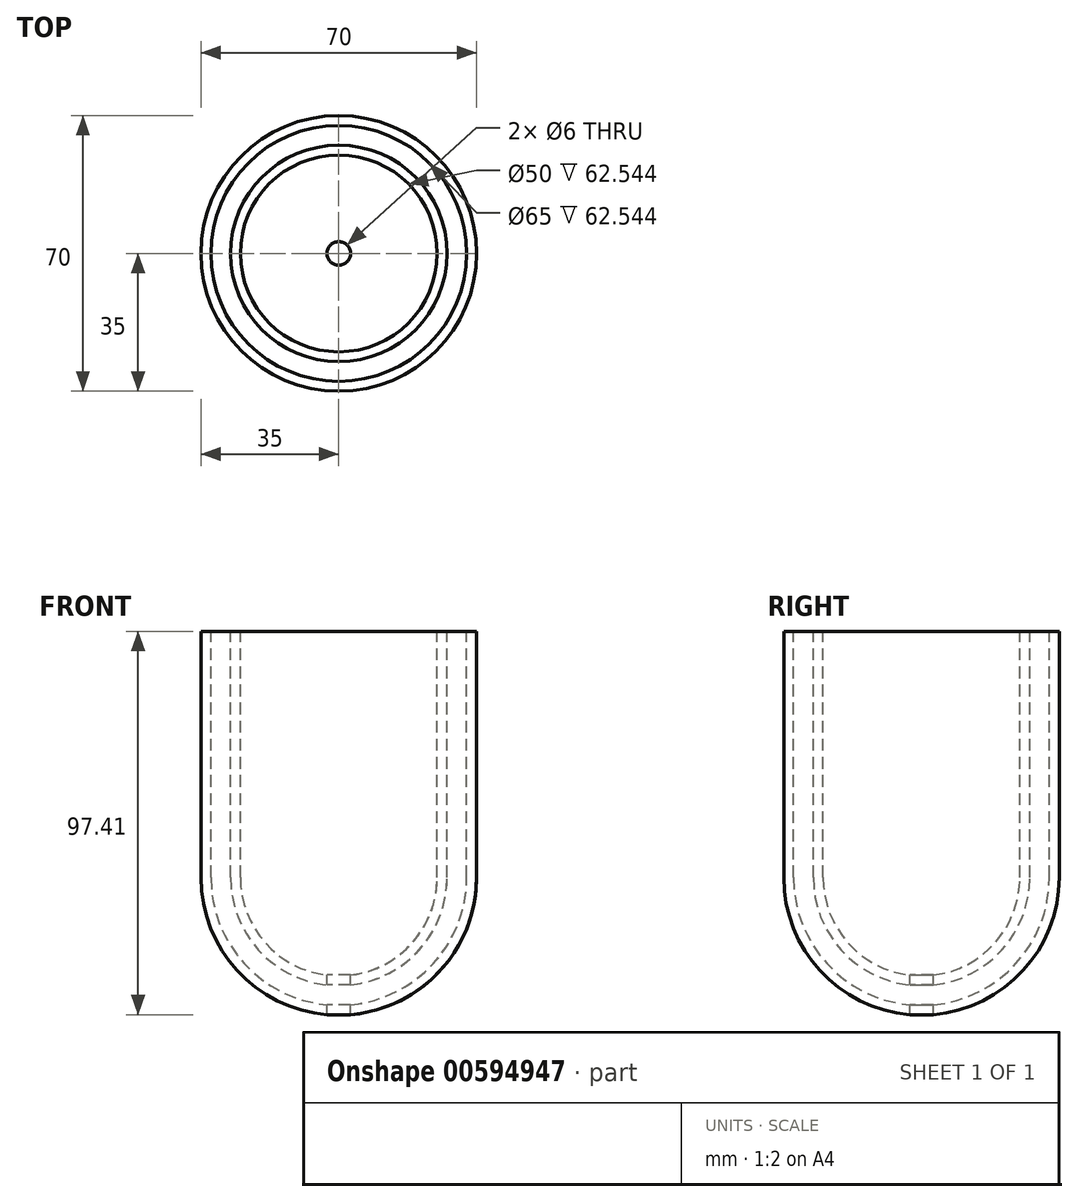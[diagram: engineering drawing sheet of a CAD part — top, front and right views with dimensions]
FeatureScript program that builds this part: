
annotation { "Feature Type Name" : "Feature", "Feature Type Description" : "" }
export const myFeature = defineFeature(function(context is Context, id is Id, definition is map)
    precondition{}
    {
        {
            var Q0;
            Q0=qCreatedBy(makeId("Front.planeOp"),FACE);
            var sketch = newSketch(context, id + "F0", { "sketchPlane" : qUnion([Q0])});
            skCircle(sketch, "E0", {"center": v(0, 0) * mm, "radius": 32.5 * mm, "construction": true});
            skCircle(sketch, "E1", {"center": v(0, 0) * mm, "radius": 35 * mm, "construction": true});
            skCircle(sketch, "E2", {"center": v(0, 0) * mm, "radius": 25 * mm, "construction": true});
            skCircle(sketch, "E3", {"center": v(0, 0) * mm, "radius": 27.5 * mm, "construction": true});
            skArc(sketch, "E4", {"start": v(-25, 0) * mm, "mid": v(0, -25) * mm, "end": v(25, 0) * mm});
            skArc(sketch, "E5", {"start": v(-27.5, 0) * mm, "mid": v(0, -27.5) * mm, "end": v(27.5, 0) * mm});
            skArc(sketch, "E6", {"start": v(-32.5, 0) * mm, "mid": v(0, -32.5) * mm, "end": v(32.5, 0) * mm});
            skArc(sketch, "E7", {"start": v(-35, 0) * mm, "mid": v(0, -35) * mm, "end": v(35, 0) * mm});
            skLineSegment(sketch, "E8", {"start": v(-35, 0) * mm, "end": v(-35, 62.54) * mm});
            skLineSegment(sketch, "E9", {"start": v(-32.5, 0) * mm, "end": v(-32.5, 62.54) * mm});
            skLineSegment(sketch, "E10", {"start": v(-27.5, 0) * mm, "end": v(-27.5, 62.54) * mm});
            skLineSegment(sketch, "E11", {"start": v(-25, 0) * mm, "end": v(-25, 62.54) * mm});
            skLineSegment(sketch, "E12", {"start": v(25, 0) * mm, "end": v(25, 62.54) * mm});
            skLineSegment(sketch, "E13", {"start": v(27.5, 0) * mm, "end": v(27.5, 62.54) * mm});
            skLineSegment(sketch, "E14", {"start": v(32.5, 0) * mm, "end": v(32.5, 62.54) * mm});
            skLineSegment(sketch, "E15", {"start": v(35, 0) * mm, "end": v(35, 62.63) * mm});
            skPoint(sketch, "E16", {"position": v(0, -25) * mm});
            skPoint(sketch, "E17", {"position": v(0, -27.5) * mm});
            skPoint(sketch, "E18", {"position": v(0, -32.5) * mm});
            skPoint(sketch, "E19", {"position": v(0, -35) * mm});
            skLineSegment(sketch, "E20.bottom", {"start": v(-3, -16) * mm, "end": v(3, -16) * mm});
            skLineSegment(sketch, "E20.top", {"start": v(-3, -42) * mm, "end": v(3, -42) * mm});
            skLineSegment(sketch, "E20.left", {"start": v(-3, -16) * mm, "end": v(-3, -42) * mm});
            skLineSegment(sketch, "E20.right", {"start": v(3, -16) * mm, "end": v(3, -42) * mm});
            skLineSegment(sketch, "E21", {"start": v(-35, 62.54) * mm, "end": v(35, 62.54) * mm});
            skLineSegment(sketch, "E22", {"start": v(-35, 57.54) * mm, "end": v(35, 57.54) * mm});
            skLineSegment(sketch, "E23", {"start": v(0, 100.78) * mm, "end": v(0, -81.22) * mm, "construction": true});
            skPoint(sketch, "E23.startSnap0", {"position": v(0, 62.54) * mm});
            skArc(sketch, "E24", {"start": v(-35, 62.54) * mm, "mid": v(0, 97.54) * mm, "end": v(35, 62.54) * mm});
            skArc(sketch, "E25", {"start": v(-25, 62.54) * mm, "mid": v(0, 87.54) * mm, "end": v(25, 62.54) * mm});
            skArc(sketch, "E26", {"start": v(-27.5, 62.54) * mm, "mid": v(0, 90.04) * mm, "end": v(27.5, 62.54) * mm});
            skArc(sketch, "E27", {"start": v(32.5, 62.54) * mm, "mid": v(0, 95.04) * mm, "end": v(-32.5, 62.54) * mm});
            skPoint(sketch, "E28", {"position": v(0, 97.54) * mm});
            skPoint(sketch, "E29", {"position": v(0, 95.04) * mm});
            skPoint(sketch, "E30", {"position": v(0, 90.04) * mm});
            skPoint(sketch, "E31", {"position": v(0, 87.54) * mm});
            skSolve(sketch);
        }
        {
            var Q0;
            {var subQ1=sQuery(id+"F0.wireOp",EDGE,"E10");var subQ3=sQuery(id+"F0.wireOp",EDGE,"E22");var subQ4=makeQuery(id+"F0.imprint","INTERSECT",VERTEX,{"derivedFrom":[subQ1,subQ3]});Q0=makeQuery(id+"F0.imprint","IMPRINT",FACE,{"disambiguationData":[TD([[makeQuery(id+"F0.imprint","IMPRINT",EDGE,{"disambiguationData":[TD([[subQ4,-1.0]])],"derivedFrom":subQ3}),1.0]])]});}
            var Q1;
            {var subQ5=sQuery(id+"F0.wireOp",EDGE,"E11");var subQ7=sQuery(id+"F0.wireOp",EDGE,"E4");var subQ8=makeQuery(id+"F0.imprint","INTERSECT",VERTEX,{"derivedFrom":[subQ7,subQ5]});Q1=makeQuery(id+"F0.imprint","IMPRINT",FACE,{"disambiguationData":[TD([[makeQuery(id+"F0.imprint","IMPRINT",EDGE,{"disambiguationData":[TD([[subQ8,-1.0]])],"derivedFrom":subQ7}),-1.0]])]});}
            var Q2;
            {var subQ1=sQuery(id+"F0.wireOp",EDGE,"E8");var subQ3=sQuery(id+"F0.wireOp",EDGE,"E22");var subQ4=makeQuery(id+"F0.imprint","INTERSECT",VERTEX,{"derivedFrom":[subQ1,subQ3]});Q2=makeQuery(id+"F0.imprint","IMPRINT",FACE,{"disambiguationData":[TD([[makeQuery(id+"F0.imprint","IMPRINT",EDGE,{"disambiguationData":[TD([[subQ4,-1.0]])],"derivedFrom":subQ3}),1.0]])]});}
            var Q3;
            {var subQ5=sQuery(id+"F0.wireOp",EDGE,"E9");var subQ6=sQuery(id+"F0.wireOp",EDGE,"E6");var subQ7=makeQuery(id+"F0.imprint","INTERSECT",VERTEX,{"derivedFrom":[subQ6,subQ5]});Q3=makeQuery(id+"F0.imprint","IMPRINT",FACE,{"disambiguationData":[TD([[makeQuery(id+"F0.imprint","IMPRINT",EDGE,{"disambiguationData":[TD([[subQ7,-1.0]])],"derivedFrom":subQ6}),-1.0]])]});}
            var Q4;
            Q4=sQuery(id+"F0.wireOp",EDGE,"E23");
            revolve(context, id + "F1", {"entities" : qUnion([Q0, Q1, Q2, Q3]), "axis" : qUnion([Q4]), "revolveType" : RevolveType.FULL});
        }
    });
